# Revit family: P200635WX-057c_WCE55US0HS
name_source: partatom
category: Specialty Equipment
units: mm (PartAtom-declared; Revit-internal decimal feet)

## family parameters
Always vertical = Yes
Cut with Voids When Loaded = No
Enable Cutting in Views = No
Maintain Annotation Orientation = No
Part Type = Normal
Room Calculation Point = No
Round Connector Dimension = Use Diameter
Shared = No
Work Plane-Based = No

## types (1)
- WCE55US0HS
    Amps = 0 A
    Body Material = ARCAT - Metal - Steel - Stainless
    Cooking Grate Material = ARCAT - Metal - Cast Iron 1/4" Plate
    Cooktop Material = ARCAT - Glass - Tempered - Black
    Default Elevation = 0"
    Depth = 21 3/4"
    Description = "30-inch Electric Ceramic Glass Cooktop with Dual Radiant Element
Table de cuisson électrique en vitrocéramique avec élément radiant double, 30 po"
    Family Name = Electric Cooktop
    Feature 1 = "FlexHeat™ Dual Radiant Element
FlexHeat™ Dual Radiant Element"
    Feature 2 = "Easy-Wipe Ceramic Glass Cooktop
Easy-Wipe Ceramic Glass Cooktop"
    Feature 3 = "30 & 40 Amp Installation
30 & 40 Amp Installation"
    Height = 5 1/4"
    Installation-Fabrication = "https://www.whirlpool.com
http://access.whirlpool.com Instruction&sku=WCE55US0HB&language=FR"
    Knob Material = ARCAT - Metal - Steel - Stainless
    Manufacturer = Whirlpool
    Model = WCE55US0HS
    Voltage = 0 V
    Width = 30 13/16"

## geometry (parser evidence)
native form markers: Sweep x4
no freeform markers — native parametric forms only
